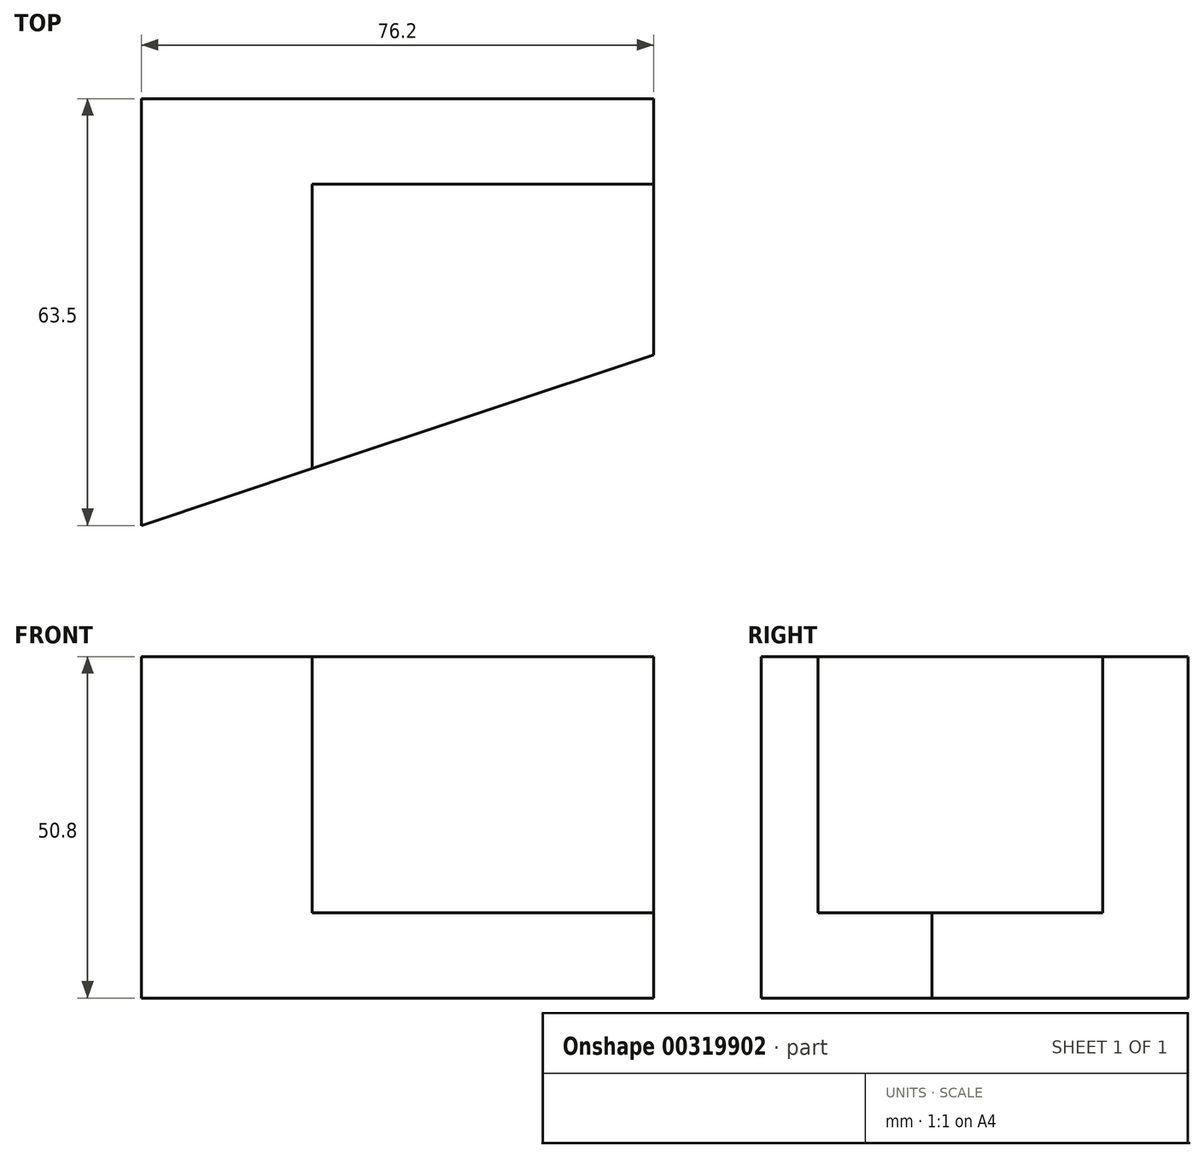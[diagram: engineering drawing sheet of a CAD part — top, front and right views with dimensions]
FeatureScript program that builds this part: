
annotation { "Feature Type Name" : "Feature", "Feature Type Description" : "" }
export const myFeature = defineFeature(function(context is Context, id is Id, definition is map)
    precondition{}
    {
        {
            var Q0;
            Q0=qCreatedBy(makeId("Front.planeOp"),FACE);
            var sketch = newSketch(context, id + "F0", { "sketchPlane" : qUnion([Q0])});
            skLineSegment(sketch, "E0", {"start": v(0, 0) * mm, "end": v(0, 50.8) * mm});
            skLineSegment(sketch, "E1", {"start": v(0, 50.8) * mm, "end": v(76.2, 50.8) * mm});
            skLineSegment(sketch, "E2", {"start": v(76.2, 50.8) * mm, "end": v(76.2, 0) * mm});
            skLineSegment(sketch, "E3", {"start": v(76.2, 0) * mm, "end": v(0, 0) * mm});
            skLineSegment(sketch, "E4", {"start": v(0, 50.8) * mm, "end": v(25.4, 50.8) * mm});
            skLineSegment(sketch, "E5", {"start": v(25.4, 50.8) * mm, "end": v(25.4, 12.7) * mm});
            skLineSegment(sketch, "E6", {"start": v(25.4, 12.7) * mm, "end": v(76.2, 12.7) * mm});
            skSolve(sketch);
        }
        {
            var Q0;
            Q0 = qSketchRegion(id + "F0", true);
            extrude(context, id + "F1", {"entities" : qUnion([Q0]), "depth" : 63.5 * mm});
        }
        {
            var Q0;
            Q0=makeQuery(id+"F1.opExtrude","SWEPT_FACE",FACE,{"disambiguationData":[OSD([sQuery(id+"F0.wireOp",EDGE,"E1"),sQuery(id+"F0.wireOp",EDGE,"E4")])]});
            var sketch = newSketch(context, id + "F2", { "sketchPlane" : qUnion([Q0])});
            skLineSegment(sketch, "E7", {"start": v(0, 0) * mm, "end": v(76.2, 0) * mm});
            skLineSegment(sketch, "E8", {"start": v(76.2, 0) * mm, "end": v(76.2, -12.7) * mm});
            skLineSegment(sketch, "E9", {"start": v(76.2, -12.7) * mm, "end": v(25.4, -12.7) * mm});
            skLineSegment(sketch, "E10", {"start": v(76.2, 0) * mm, "end": v(76.2, -38.1) * mm});
            skLineSegment(sketch, "E11", {"start": v(76.2, -38.1) * mm, "end": v(0, -63.5) * mm});
            skLineSegment(sketch, "E12", {"start": v(0, -63.5) * mm, "end": v(0, 0) * mm});
            skLineSegment(sketch, "E13", {"start": v(25.4, -12.7) * mm, "end": v(25.4, -55.03) * mm});
            skSolve(sketch);
        }
        {
            var Q0;
            {var subQ1=sQuery(id+"F0.wireOp",EDGE,"E1");var subQ5=makeQuery(id+"F1.opExtrude","CAP_EDGE",EDGE,{"disambiguationData":[OSD([subQ1,sQuery(id+"F0.wireOp",EDGE,"E4")])],"isStart":false});Q0=makeQuery(id+"F2.imprint","IMPRINT",FACE,{"disambiguationData":[TD([[makeQuery(id+"F2.imprint","IMPRINT",EDGE,{"derivedFrom":subQ5}),1.0]])]});}
            extrude(context, id + "F3", {"entities" : qUnion([Q0]), "operationType" : NewBodyOperationType.REMOVE, "endBound" : BoundingType.THROUGH_ALL, "oppositeDirection" : true, "depth" : 25.4 * mm});
        }
        {
            var Q0;
            {var subQ0=sQuery(id+"F2.wireOp",EDGE,"E9");Q0=makeQuery(id+"F2.imprint","IMPRINT",FACE,{"disambiguationData":[TD([[makeQuery(id+"F2.imprint","IMPRINT",EDGE,{"derivedFrom":subQ0}),1.0]])]});}
            extrude(context, id + "F4", {"entities" : qUnion([Q0]), "operationType" : NewBodyOperationType.REMOVE, "oppositeDirection" : true, "depth" : 38.1 * mm});
        }
    });
